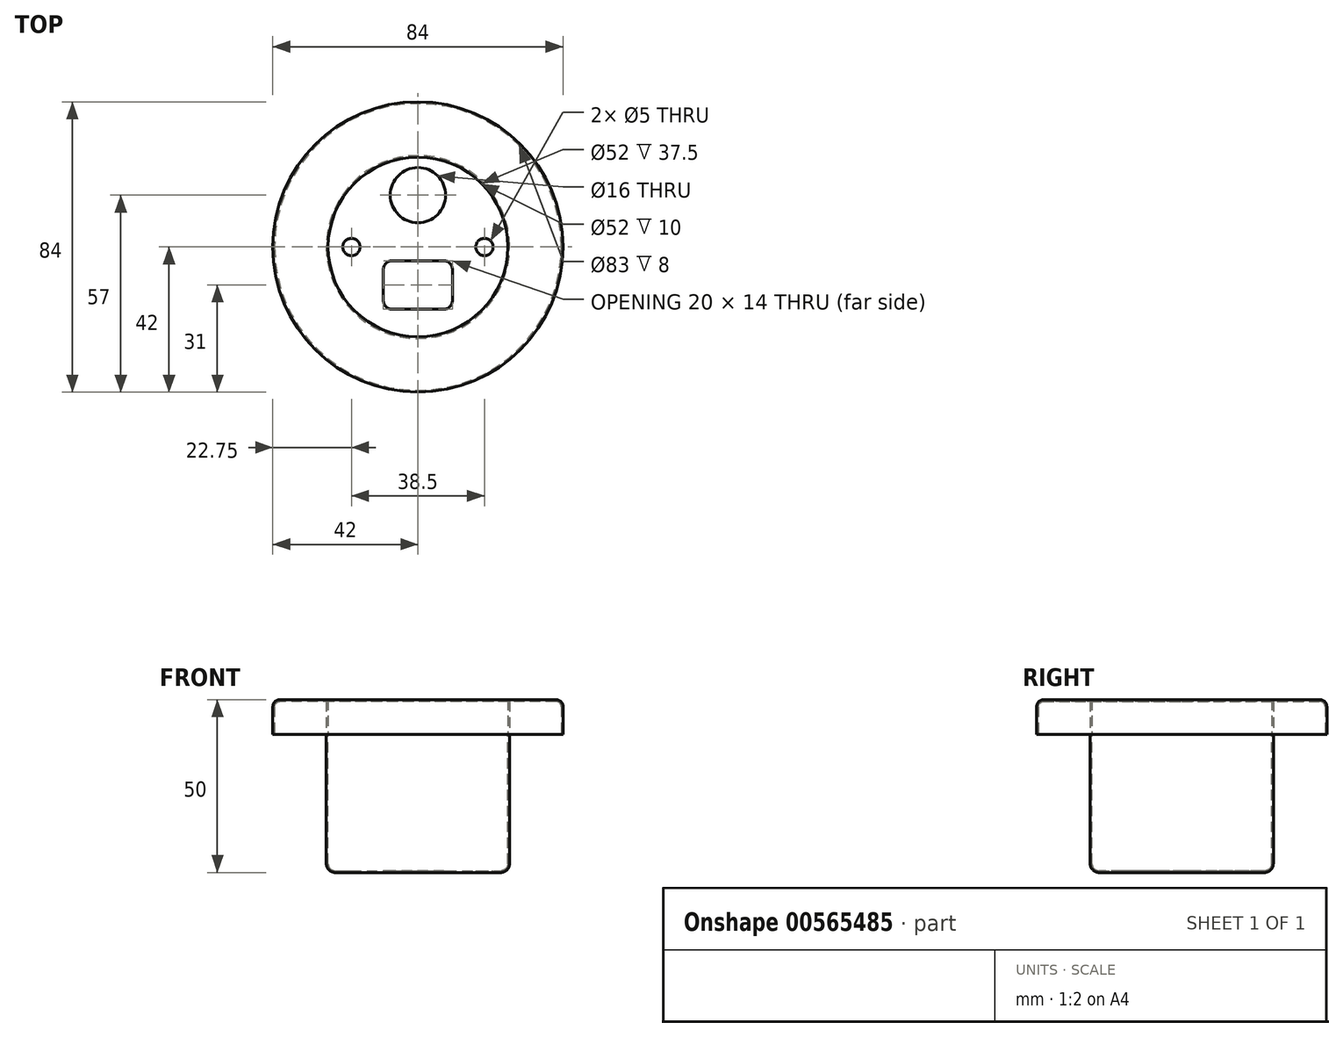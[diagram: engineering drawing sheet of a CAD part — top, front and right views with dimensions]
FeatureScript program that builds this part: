
annotation { "Feature Type Name" : "Feature", "Feature Type Description" : "" }
export const myFeature = defineFeature(function(context is Context, id is Id, definition is map)
    precondition{}
    {
        {
            var Q0;
            Q0=qCreatedBy(makeId("Top.planeOp"),FACE);
            var sketch = newSketch(context, id + "F0", { "sketchPlane" : qUnion([Q0])});
            skCircle(sketch, "E0", {"center": v(0, 0) * mm, "radius": 42 * mm});
            skCircle(sketch, "E1", {"center": v(0, 0) * mm, "radius": 26 * mm});
            skSolve(sketch);
        }
        {
            var Q0;
            Q0=makeQuery(id+"F0.imprint","IMPRINT",FACE,{"disambiguationData":[TD([[makeQuery(id+"F0.imprint","IMPRINT",EDGE,{"derivedFrom":sQuery(id+"F0.wireOp",EDGE,"E0")}),1.0]])]});
            extrude(context, id + "F1", {"entities" : qUnion([Q0]), "depth" : 10 * mm, "offsetDistance" : 25 * mm});
        }
        {
            var Q0;
            Q0=makeQuery(id+"F1.opExtrude","CAP_EDGE",EDGE,{"disambiguationData":[OSD([sQuery(id+"F0.wireOp",EDGE,"E0")])],"isStart":false});
            fillet(context, id + "F2", {"entities" : qUnion([Q0]), "radius" : 2 * mm, "tangentPropagation" : true, "allowEdgeOverflow" : false});
        }
        {
            var Q0;
            Q0=makeQuery(id+"F1.opExtrude","CAP_FACE",FACE,{"disambiguationData":[OSD([sQuery(id+"F0.wireOp",EDGE,"E0"),sQuery(id+"F0.wireOp",EDGE,"E1")])],"isStart":true});
            var sketch = newSketch(context, id + "F3", { "sketchPlane" : qUnion([Q0])});
            skCircle(sketch, "E2", {"center": v(0, 0) * mm, "radius": 26.5 * mm});
            skSolve(sketch);
        }
        {
            var Q0;
            Q0=qSketchRegion(id+"F3",true);
            extrude(context, id + "F4", {"entities" : qUnion([Q0]), "depth" : 40 * mm, "offsetDistance" : 25 * mm});
        }
        {
            var Q0;
            Q0=makeQuery(id+"F4.opExtrude","CAP_EDGE",EDGE,{"disambiguationData":[OSD([sQuery(id+"F3.wireOp",EDGE,"E2")])],"isStart":false});
            fillet(context, id + "F5", {"entities" : qUnion([Q0]), "radius" : 2.5 * mm, "tangentPropagation" : true, "allowEdgeOverflow" : false});
        }
        {
            var Q0;
            Q0=makeQuery(id+"F4.opExtrude","CAP_FACE",FACE,{"disambiguationData":[OSD([sQuery(id+"F3.wireOp",EDGE,"E2")])],"isStart":true});
            shell(context, id + "F6", {"entities" : qUnion([Q0]), "thickness" : .5 * mm});
        }
        {
            var Q0;
            Q0=makeQuery(id+"F1.opExtrude","CAP_FACE",FACE,{"disambiguationData":[OSD([sQuery(id+"F0.wireOp",EDGE,"E0"),sQuery(id+"F0.wireOp",EDGE,"E1")])],"isStart":true});
            shell(context, id + "F7", {"entities" : qUnion([Q0]), "thickness" : .5 * mm});
        }
        {
            var Q0;
            Q0=makeQuery(id+"F4.opExtrude","CAP_FACE",FACE,{"disambiguationData":[OSD([sQuery(id+"F3.wireOp",EDGE,"E2")])],"isStart":false});
            var sketch = newSketch(context, id + "F8", { "sketchPlane" : qUnion([Q0])});
            skLineSegment(sketch, "E3.bottom", {"start": v(7.5, 4) * mm, "end": v(-7.5, 4) * mm});
            skLineSegment(sketch, "E3.top", {"start": v(7.5, 18) * mm, "end": v(-7.5, 18) * mm});
            skLineSegment(sketch, "E3.left", {"start": v(10, 6.5) * mm, "end": v(10, 15.5) * mm});
            skLineSegment(sketch, "E3.right", {"start": v(-10, 6.5) * mm, "end": v(-10, 15.5) * mm});
            skPoint(sketch, "E3.middle", {"position": v(0, 11) * mm});
            skLineSegment(sketch, "E4", {"start": v(-10, 11) * mm, "end": v(10, 11) * mm, "construction": true});
            skPoint(sketch, "E5.visualSharp", {"position": v(-10, 18) * mm});
            skArc(sketch, "E5.filletArc", {"start": v(-7.5, 18) * mm, "mid": v(-9.27, 17.27) * mm, "end": v(-10, 15.5) * mm});
            skPoint(sketch, "E6.visualSharp", {"position": v(10, 18) * mm});
            skArc(sketch, "E6.filletArc", {"start": v(10, 15.5) * mm, "mid": v(9.27, 17.27) * mm, "end": v(7.5, 18) * mm});
            skPoint(sketch, "E7.visualSharp", {"position": v(10, 4) * mm});
            skArc(sketch, "E7.filletArc", {"start": v(7.5, 4) * mm, "mid": v(9.27, 4.73) * mm, "end": v(10, 6.5) * mm});
            skPoint(sketch, "E8.visualSharp", {"position": v(-10, 4) * mm});
            skArc(sketch, "E8.filletArc", {"start": v(-10, 6.5) * mm, "mid": v(-9.27, 4.73) * mm, "end": v(-7.5, 4) * mm});
            skCircle(sketch, "E9", {"center": v(0, -15) * mm, "radius": 8 * mm});
            skCircle(sketch, "E10", {"center": v(-19.25, 0) * mm, "radius": 2.5 * mm});
            skCircle(sketch, "E11", {"center": v(19.25, 0) * mm, "radius": 2.5 * mm});
            skSolve(sketch);
        }
        {
            var Q0;
            Q0 = qSketchRegion(id + "F8", true);
            extrude(context, id + "F9", {"entities" : qUnion([Q0]), "operationType" : NewBodyOperationType.REMOVE, "oppositeDirection" : true, "depth" : 25 * mm, "offsetDistance" : 25 * mm});
        }
    });
